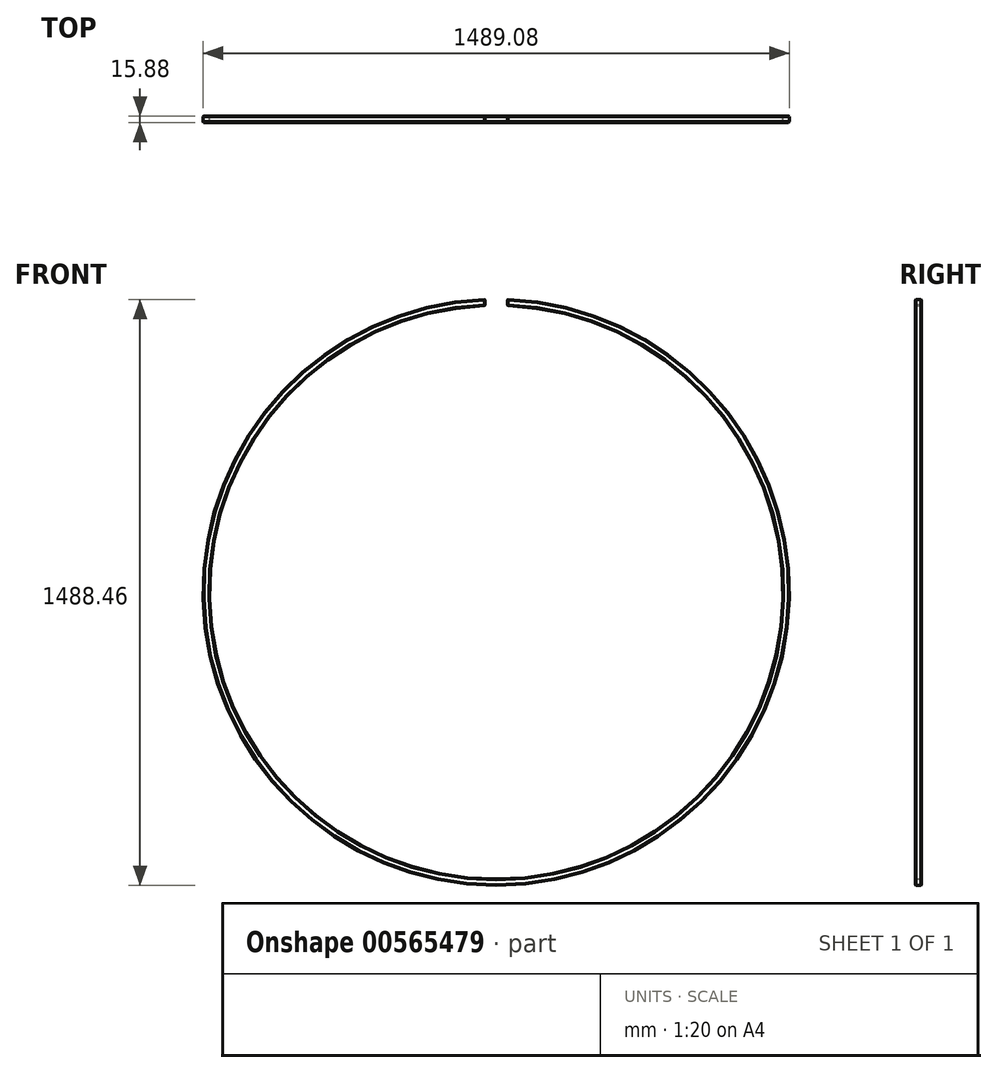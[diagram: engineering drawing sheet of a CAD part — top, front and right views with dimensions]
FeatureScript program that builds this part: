
annotation { "Feature Type Name" : "Feature", "Feature Type Description" : "" }
export const myFeature = defineFeature(function(context is Context, id is Id, definition is map)
    precondition{}
    {
        {
            var Q0;
            Q0=qCreatedBy(makeId("Front.planeOp"),FACE);
            var sketch = newSketch(context, id + "F0", { "sketchPlane" : qUnion([Q0])});
            skArc(sketch, "E0", {"start": v(-28.58, 743.99) * mm, "mid": v(0, -744.54) * mm, "end": v(28.57, 743.99) * mm});
            skArc(sketch, "E1", {"start": v(-28.58, 728.1) * mm, "mid": v(0, -728.66) * mm, "end": v(28.58, 728.1) * mm});
            skLineSegment(sketch, "E2", {"start": v(0, 0) * mm, "end": v(0, 842.58) * mm, "construction": true});
            skLineSegment(sketch, "E3.0", {"start": v(28.58, 728.1) * mm, "end": v(28.58, 743.99) * mm});
            skLineSegment(sketch, "E4.0", {"start": v(-28.58, 728.1) * mm, "end": v(-28.58, 743.99) * mm});
            skSolve(sketch);
        }
        {
            var Q0;
            Q0 = qSketchRegion(id + "F0", true);
            extrude(context, id + "F1", {"entities" : qUnion([Q0]), "depth" : 15.88 * mm, "offsetDistance" : 25.4 * mm});
        }
        {
            var Q0;
            Q0=makeQuery(id+"F1.opExtrude","SWEPT_FACE",FACE,{"disambiguationData":[OSD([sQuery(id+"F0.wireOp",EDGE,"E3.0")])]});
            var Q1;
            Q1=makeQuery(id+"F1.opExtrude","CAP_EDGE",EDGE,{"disambiguationData":[OSD([sQuery(id+"F0.wireOp",EDGE,"E1")])],"isStart":true});
            var Q2;
            Q2=makeQuery(id+"F1.opExtrude","CAP_EDGE",EDGE,{"disambiguationData":[OSD([sQuery(id+"F0.wireOp",EDGE,"E0")])],"isStart":true});
            var Q3;
            Q3=makeQuery(id+"F1.opExtrude","CAP_EDGE",EDGE,{"disambiguationData":[OSD([sQuery(id+"F0.wireOp",EDGE,"E0")])],"isStart":false});
            var Q4;
            Q4=makeQuery(id+"F1.opExtrude","CAP_EDGE",EDGE,{"disambiguationData":[OSD([sQuery(id+"F0.wireOp",EDGE,"E1")])],"isStart":false});
            var Q5;
            Q5=makeQuery(id+"F1.opExtrude","SWEPT_FACE",FACE,{"disambiguationData":[OSD([sQuery(id+"F0.wireOp",EDGE,"E4.0")])]});
            chamfer(context, id + "F2", {"entities" : qUnion([Q0, Q1, Q2, Q3, Q4, Q5]), "width" : 1.59 * mm, "tangentPropagation" : true});
        }
    });
